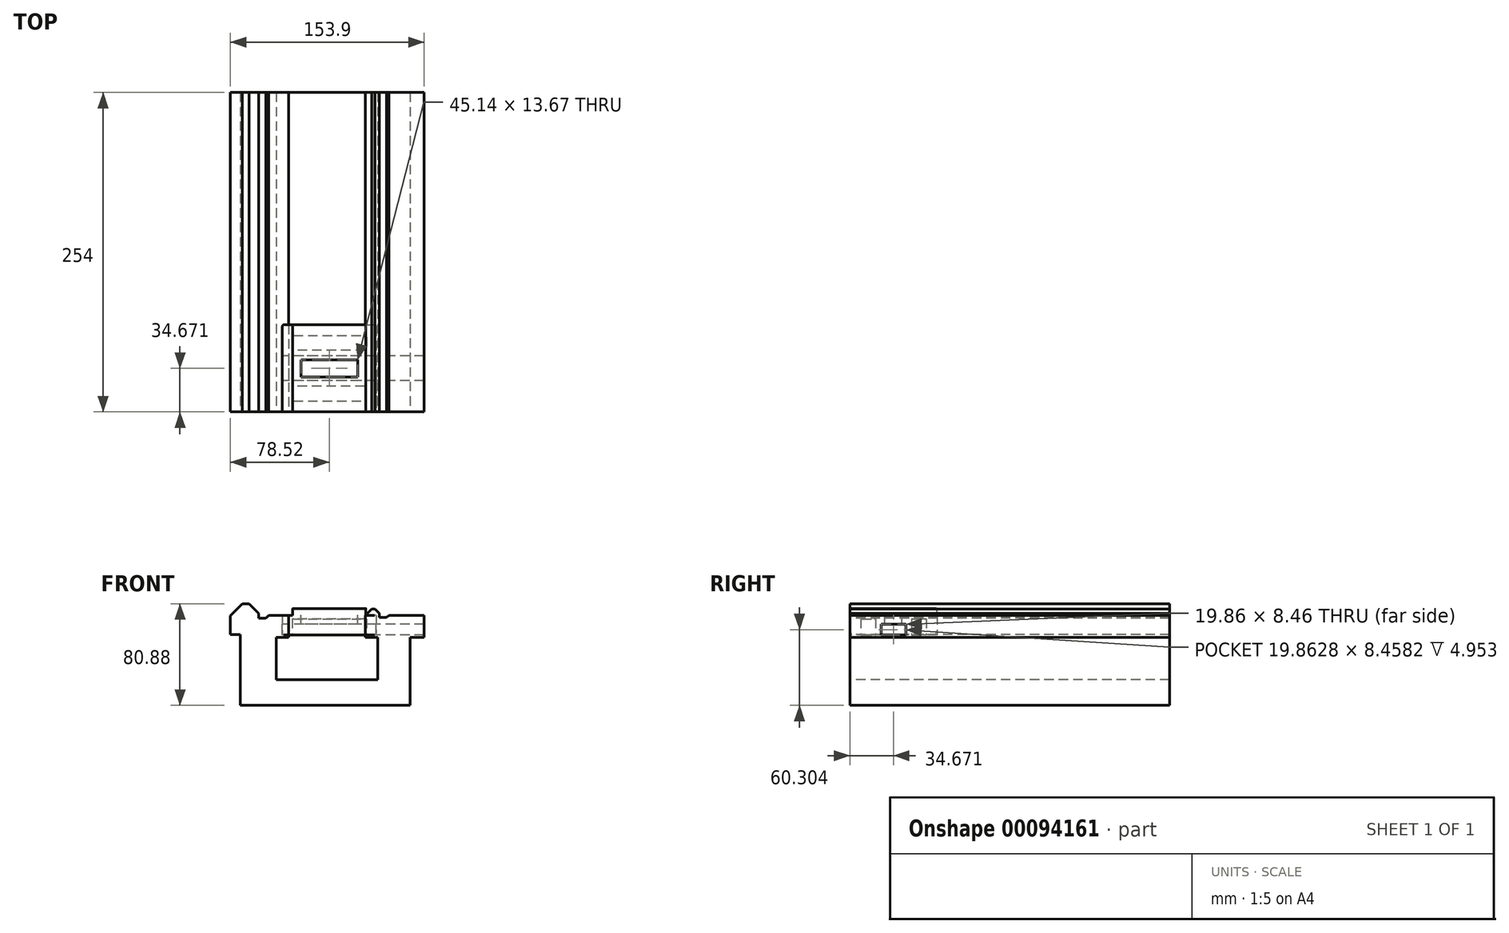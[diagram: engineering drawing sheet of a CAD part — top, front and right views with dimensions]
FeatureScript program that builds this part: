
annotation { "Feature Type Name" : "Feature", "Feature Type Description" : "" }
export const myFeature = defineFeature(function(context is Context, id is Id, definition is map)
    precondition{}
    {
        {
            var Q0;
            Q0=qCreatedBy(makeId("Front.planeOp"),FACE);
            var sketch = newSketch(context, id + "F0", { "sketchPlane" : qUnion([Q0])});
            skLineSegment(sketch, "E0", {"start": v(28.67, -0.1) * mm, "end": v(28.67, -17.38) * mm, "construction": true});
            skLineSegment(sketch, "E1", {"start": v(-32.32, -0.14) * mm, "end": v(-32.17, -17.38) * mm});
            skLineSegment(sketch, "E2", {"start": v(-32.17, -17.38) * mm, "end": v(-42.05, -17.38) * mm});
            skLineSegment(sketch, "E3", {"start": v(-32.32, -0.14) * mm, "end": v(-48.22, -0.14) * mm});
            skLineSegment(sketch, "E4", {"start": v(-48.22, -0.14) * mm, "end": v(-50.4, -2.17) * mm});
            skLineSegment(sketch, "E5", {"start": v(-50.4, -2.17) * mm, "end": v(-56.12, -2.17) * mm});
            skLineSegment(sketch, "E6", {"start": v(-56.12, -2.17) * mm, "end": v(-56.12, 1.62) * mm});
            skLineSegment(sketch, "E7", {"start": v(-56.12, 1.62) * mm, "end": v(-63.76, 9.26) * mm});
            skLineSegment(sketch, "E8", {"start": v(-70.74, -15.12) * mm, "end": v(-78.52, -15.12) * mm});
            skLineSegment(sketch, "E9", {"start": v(-69, 9.26) * mm, "end": v(-63.76, 9.26) * mm, "construction": true});
            skLineSegment(sketch, "E10", {"start": v(-63.76, 9.26) * mm, "end": v(-69, 9.26) * mm});
            skLineSegment(sketch, "E11", {"start": v(-69, 9.26) * mm, "end": v(-78.52, -0.27) * mm});
            skLineSegment(sketch, "E12", {"start": v(-70.74, -15.12) * mm, "end": v(-70.74, -40.32) * mm});
            skLineSegment(sketch, "E13", {"start": v(28.67, -17.38) * mm, "end": v(38.52, -17.38) * mm, "construction": true});
            skLineSegment(sketch, "E14", {"start": v(33.66, 4.9) * mm, "end": v(36.3, 4.9) * mm, "construction": true});
            skLineSegment(sketch, "E15", {"start": v(39.74, -1.69) * mm, "end": v(39.74, 1.46) * mm, "construction": true});
            skLineSegment(sketch, "E16", {"start": v(45.6, -1.69) * mm, "end": v(39.74, -1.69) * mm, "construction": true});
            skLineSegment(sketch, "E17", {"start": v(28.67, -17.38) * mm, "end": v(38.52, -17.38) * mm});
            skLineSegment(sketch, "E18", {"start": v(38.52, -17.38) * mm, "end": v(38.52, -19.45) * mm});
            skLineSegment(sketch, "E19", {"start": v(28.67, -17.38) * mm, "end": v(28.67, -0.1) * mm});
            skLineSegment(sketch, "E20", {"start": v(33.66, 4.9) * mm, "end": v(36.3, 4.9) * mm});
            skLineSegment(sketch, "E21", {"start": v(39.74, 1.46) * mm, "end": v(39.74, -1.69) * mm});
            skLineSegment(sketch, "E22", {"start": v(39.74, -1.69) * mm, "end": v(45.6, -1.69) * mm});
            skLineSegment(sketch, "E23", {"start": v(75.38, -1.69) * mm, "end": v(75.38, -17.38) * mm});
            skLineSegment(sketch, "E24", {"start": v(75.38, -17.38) * mm, "end": v(64.28, -17.38) * mm});
            skLineSegment(sketch, "E25", {"start": v(64.28, -17.38) * mm, "end": v(64.28, -37.3) * mm});
            skLineSegment(sketch, "E26", {"start": v(64.28, -37.3) * mm, "end": v(64.28, -51.73) * mm});
            skLineSegment(sketch, "E27", {"start": v(-70.74, -51.73) * mm, "end": v(-70.74, -40.32) * mm});
            skLineSegment(sketch, "E28", {"start": v(38.52, -19.45) * mm, "end": v(38.52, -51.23) * mm});
            skLineSegment(sketch, "E29", {"start": v(38.52, -51.23) * mm, "end": v(-42.05, -51.23) * mm});
            skLineSegment(sketch, "E30", {"start": v(-42.05, -51.23) * mm, "end": v(-42.05, -17.38) * mm});
            skLineSegment(sketch, "E31", {"start": v(-70.74, -51.73) * mm, "end": v(-70.74, -71.62) * mm});
            skLineSegment(sketch, "E32", {"start": v(-70.74, -71.62) * mm, "end": v(64.28, -71.62) * mm});
            skLineSegment(sketch, "E33", {"start": v(64.28, -71.62) * mm, "end": v(64.28, -51.73) * mm});
            skPoint(sketch, "E34.orphan", {"position": v(18.52, -51.23) * mm});
            skLineSegment(sketch, "E35.trimOffspring", {"start": v(64.28, -17.38) * mm, "end": v(75.38, -17.38) * mm, "construction": true});
            skLineSegment(sketch, "E36", {"start": v(33.66, 4.9) * mm, "end": v(28.67, -0.1) * mm});
            skLineSegment(sketch, "E37", {"start": v(36.3, 4.9) * mm, "end": v(39.74, 1.46) * mm});
            skPoint(sketch, "E38", {"position": v(28.67, -0.1) * mm});
            skPoint(sketch, "E39", {"position": v(39.74, 1.46) * mm});
            skLineSegment(sketch, "E40", {"start": v(45.6, -1.69) * mm, "end": v(47.3, 0.02) * mm});
            skLineSegment(sketch, "E41", {"start": v(73.53, 0.02) * mm, "end": v(47.3, 0.02) * mm});
            skLineSegment(sketch, "E42", {"start": v(75.38, -1.69) * mm, "end": v(75.38, 0.02) * mm});
            skLineSegment(sketch, "E43", {"start": v(75.38, 0.02) * mm, "end": v(73.53, 0.02) * mm});
            skLineSegment(sketch, "E44", {"start": v(-78.52, -15.12) * mm, "end": v(-78.52, -0.27) * mm});
            skSolve(sketch);
        }
        {
            var Q0;
            Q0=makeQuery(id+"F0.imprint","IMPRINT",FACE,{"disambiguationData":[TD([[makeQuery(id+"F0.imprint","IMPRINT",EDGE,{"derivedFrom":sQuery(id+"F0.wireOp",EDGE,"E1")}),-1.0]])]});
            extrude(context, id + "F1", {"entities" : qUnion([Q0]), "oppositeDirection" : true, "depth" : 254 * mm});
        }
        {
            var Q0;
            Q0=qCreatedBy(makeId("Front.planeOp"),FACE);
            var sketch = newSketch(context, id + "F2", { "sketchPlane" : qUnion([Q0])});
            skPoint(sketch, "E45.middle", {"position": v(0, 0) * mm});
            skLineSegment(sketch, "E46.bottom", {"start": v(-37.21, 0) * mm, "end": v(-29.08, 0) * mm});
            skLineSegment(sketch, "E46.top", {"start": v(-37.21, -15.54) * mm, "end": v(37.21, -15.54) * mm});
            skLineSegment(sketch, "E46.left", {"start": v(-37.21, 0) * mm, "end": v(-37.21, -15.54) * mm});
            skLineSegment(sketch, "E46.right", {"start": v(37.21, 0) * mm, "end": v(37.21, -15.54) * mm});
            skLineSegment(sketch, "E47.top", {"start": v(-29.08, 5.38) * mm, "end": v(29.08, 5.38) * mm});
            skLineSegment(sketch, "E47.left", {"start": v(-29.08, 0) * mm, "end": v(-29.08, 5.38) * mm});
            skLineSegment(sketch, "E47.right", {"start": v(29.08, 0) * mm, "end": v(29.08, 5.38) * mm});
            skLineSegment(sketch, "E48.trimOffspring", {"start": v(29.08, 0) * mm, "end": v(37.21, 0) * mm});
            skSolve(sketch);
        }
        {
            var Q0;
            Q0=makeQuery(id+"F2.imprint","IMPRINT",FACE,{"disambiguationData":[TD([[makeQuery(id+"F2.imprint","IMPRINT",EDGE,{"derivedFrom":sQuery(id+"F2.wireOp",EDGE,"E46.bottom")}),-1.0]])]});
            extrude(context, id + "F3", {"entities" : qUnion([Q0]), "oppositeDirection" : true, "depth" : 69.34 * mm});
        }
        {
            var Q0;
            Q0=makeQuery(id+"F3.opExtrude","SWEPT_FACE",FACE,{"disambiguationData":[OSD([sQuery(id+"F2.wireOp",EDGE,"E46.left")])]});
            var sketch = newSketch(context, id + "F4", { "sketchPlane" : qUnion([Q0])});
            skLineSegment(sketch, "E49.bottom", {"start": v(-44.6, -15.54) * mm, "end": v(-24.74, -15.54) * mm});
            skLineSegment(sketch, "E49.top", {"start": v(-44.6, -7.09) * mm, "end": v(-24.74, -7.09) * mm});
            skLineSegment(sketch, "E49.left", {"start": v(-44.6, -15.54) * mm, "end": v(-44.6, -7.09) * mm});
            skLineSegment(sketch, "E49.right", {"start": v(-24.74, -15.54) * mm, "end": v(-24.74, -7.09) * mm});
            skPoint(sketch, "E50", {"position": v(-34.67, -15.54) * mm});
            skSolve(sketch);
        }
        {
            var Q0;
            Q0=makeQuery(id+"F4.imprint","IMPRINT",FACE,{"disambiguationData":[TD([[makeQuery(id+"F4.imprint","IMPRINT",EDGE,{"derivedFrom":sQuery(id+"F4.wireOp",EDGE,"E49.bottom")}),1.0]])]});
            extrude(context, id + "F5", {"entities" : qUnion([Q0]), "operationType" : NewBodyOperationType.REMOVE, "endBound" : BoundingType.THROUGH_ALL, "oppositeDirection" : true, "depth" : 25.4 * mm});
        }
        {
            var Q0;
            Q0=makeQuery(id+"F3.opExtrude","SWEPT_FACE",FACE,{"disambiguationData":[OSD([sQuery(id+"F2.wireOp",EDGE,"E47.top")])]});
            var sketch = newSketch(context, id + "F6", { "sketchPlane" : qUnion([Q0])});
            skLineSegment(sketch, "E51.bottom", {"start": v(22.57, 41.5) * mm, "end": v(-22.57, 41.5) * mm});
            skLineSegment(sketch, "E51.top", {"start": v(22.57, 27.84) * mm, "end": v(-22.57, 27.84) * mm});
            skLineSegment(sketch, "E51.left", {"start": v(22.57, 41.5) * mm, "end": v(22.57, 27.84) * mm});
            skLineSegment(sketch, "E51.right", {"start": v(-22.57, 41.5) * mm, "end": v(-22.57, 27.84) * mm});
            skSolve(sketch);
        }
        {
            var Q0;
            Q0=makeQuery(id+"F6.imprint","IMPRINT",FACE,{"disambiguationData":[TD([[makeQuery(id+"F6.imprint","IMPRINT",EDGE,{"derivedFrom":sQuery(id+"F6.wireOp",EDGE,"E51.bottom")}),1.0]])]});
            extrude(context, id + "F7", {"entities" : qUnion([Q0]), "operationType" : NewBodyOperationType.REMOVE, "endBound" : BoundingType.UP_TO_NEXT, "oppositeDirection" : true, "depth" : 25.4 * mm});
        }
        {
            var Q0;
            {var subQ2=sQuery(id+"F2.wireOp",EDGE,"E46.top");Q0=makeQuery(id+"F5.boolean.opBoolean","SPLIT",FACE,{"disambiguationData":[TD([makeQuery(id+"F5.opExtrude","SWEPT_FACE",FACE,{"disambiguationData":[OSD([sQuery(id+"F4.wireOp",EDGE,"E49.right")])]})])],"derivedFrom":makeQuery(id+"F3.opExtrude","SWEPT_FACE",FACE,{"disambiguationData":[OSD([subQ2])]})});}
            var sketch = newSketch(context, id + "F8", { "sketchPlane" : qUnion([Q0])});
            skLineSegment(sketch, "E52", {"start": v(29.53, -8.64) * mm, "end": v(29.53, -20.34) * mm});
            skLineSegment(sketch, "E53", {"start": v(29.53, -20.34) * mm, "end": v(-29.53, -20.34) * mm});
            skLineSegment(sketch, "E54", {"start": v(-29.53, -20.34) * mm, "end": v(-29.53, -8.64) * mm});
            skLineSegment(sketch, "E55", {"start": v(-29.53, -8.64) * mm, "end": v(29.53, -8.64) * mm});
            skPoint(sketch, "E56.end.orphan", {"position": v(-9.76, -8.64) * mm});
            skPoint(sketch, "E57.end.orphan", {"position": v(-29.53, -13.61) * mm});
            skPoint(sketch, "E58.end.orphan", {"position": v(3.76, -20.34) * mm});
            skPoint(sketch, "E59.start.orphan", {"position": v(37.21, -8.64) * mm});
            skSolve(sketch);
        }
        {
            var Q0;
            {var subQ2=sQuery(id+"F2.wireOp",EDGE,"E46.top");Q0=makeQuery(id+"F5.boolean.opBoolean","SPLIT",FACE,{"disambiguationData":[TD([makeQuery(id+"F5.opExtrude","SWEPT_FACE",FACE,{"disambiguationData":[OSD([sQuery(id+"F4.wireOp",EDGE,"E49.left")])]})])],"derivedFrom":makeQuery(id+"F3.opExtrude","SWEPT_FACE",FACE,{"disambiguationData":[OSD([subQ2])]})});}
            var sketch = newSketch(context, id + "F9", { "sketchPlane" : qUnion([Q0])});
            skLineSegment(sketch, "E60", {"start": v(-29.55, -60.77) * mm, "end": v(29.7, -60.77) * mm});
            skLineSegment(sketch, "E61", {"start": v(29.7, -48.96) * mm, "end": v(-29.55, -48.96) * mm});
            skLineSegment(sketch, "E62", {"start": v(-29.55, -48.96) * mm, "end": v(-29.55, -60.77) * mm});
            skLineSegment(sketch, "E63", {"start": v(29.7, -60.77) * mm, "end": v(29.7, -48.96) * mm});
            skSolve(sketch);
        }
        {
            var Q0;
            Q0=makeQuery(id+"F8.imprint","IMPRINT",FACE,{"disambiguationData":[TD([[makeQuery(id+"F8.imprint","IMPRINT",EDGE,{"derivedFrom":sQuery(id+"F8.wireOp",EDGE,"E52")}),-1.0]])]});
            var Q1;
            Q1=makeQuery(id+"F9.imprint","IMPRINT",FACE,{"disambiguationData":[TD([[makeQuery(id+"F9.imprint","IMPRINT",EDGE,{"derivedFrom":sQuery(id+"F9.wireOp",EDGE,"E60")}),1.0]])]});
            extrude(context, id + "F10", {"entities" : qUnion([Q0, Q1]), "operationType" : NewBodyOperationType.REMOVE, "oppositeDirection" : true, "depth" : 12.7 * mm});
        }
        {
            var Q0;
            Q0=makeQuery(id+"F10.boolean.opBoolean","COPY",EDGE,{"derivedFrom":makeQuery(id+"F10.opExtrude","SWEPT_EDGE",EDGE,{"disambiguationData":[OSD([sQuery(id+"F9.wireOp",EDGE,"E61"),sQuery(id+"F9.wireOp",EDGE,"E62")])]})});
            var Q1;
            Q1=makeQuery(id+"F10.boolean.opBoolean","COPY",EDGE,{"derivedFrom":makeQuery(id+"F10.opExtrude","SWEPT_EDGE",EDGE,{"disambiguationData":[OSD([sQuery(id+"F9.wireOp",EDGE,"E60"),sQuery(id+"F9.wireOp",EDGE,"E62")])]})});
            var Q2;
            Q2=makeQuery(id+"F10.boolean.opBoolean","COPY",EDGE,{"derivedFrom":makeQuery(id+"F10.opExtrude","SWEPT_EDGE",EDGE,{"disambiguationData":[OSD([sQuery(id+"F8.wireOp",EDGE,"E53"),sQuery(id+"F8.wireOp",EDGE,"E54")])]})});
            var Q3;
            Q3=makeQuery(id+"F10.boolean.opBoolean","COPY",EDGE,{"derivedFrom":makeQuery(id+"F10.opExtrude","SWEPT_EDGE",EDGE,{"disambiguationData":[OSD([sQuery(id+"F8.wireOp",EDGE,"E54"),sQuery(id+"F8.wireOp",EDGE,"E55")])]})});
            var Q4;
            Q4=makeQuery(id+"F10.boolean.opBoolean","COPY",EDGE,{"derivedFrom":makeQuery(id+"F10.opExtrude","SWEPT_EDGE",EDGE,{"disambiguationData":[OSD([sQuery(id+"F8.wireOp",EDGE,"E52"),sQuery(id+"F8.wireOp",EDGE,"E55")])]})});
            var Q5;
            Q5=makeQuery(id+"F10.boolean.opBoolean","COPY",EDGE,{"derivedFrom":makeQuery(id+"F10.opExtrude","SWEPT_EDGE",EDGE,{"disambiguationData":[OSD([sQuery(id+"F8.wireOp",EDGE,"E52"),sQuery(id+"F8.wireOp",EDGE,"E53")])]})});
            var Q6;
            Q6=makeQuery(id+"F10.boolean.opBoolean","COPY",EDGE,{"derivedFrom":makeQuery(id+"F10.opExtrude","SWEPT_EDGE",EDGE,{"disambiguationData":[OSD([sQuery(id+"F9.wireOp",EDGE,"E60"),sQuery(id+"F9.wireOp",EDGE,"E63")])]})});
            var Q7;
            Q7=makeQuery(id+"F10.boolean.opBoolean","COPY",EDGE,{"derivedFrom":makeQuery(id+"F10.opExtrude","SWEPT_EDGE",EDGE,{"disambiguationData":[OSD([sQuery(id+"F9.wireOp",EDGE,"E61"),sQuery(id+"F9.wireOp",EDGE,"E63")])]})});
            fillet(context, id + "F11", {"entities" : qUnion([Q0, Q1, Q2, Q3, Q4, Q5, Q6, Q7]), "radius" : 1.27 * mm, "tangentPropagation" : true, "allowEdgeOverflow" : false});
        }
        {
            var Q0;
            Q0=makeQuery(id+"F3.opExtrude","CAP_EDGE",EDGE,{"disambiguationData":[OSD([sQuery(id+"F2.wireOp",EDGE,"E46.right")])],"isStart":false});
            var Q1;
            Q1=makeQuery(id+"F3.opExtrude","CAP_EDGE",EDGE,{"disambiguationData":[OSD([sQuery(id+"F2.wireOp",EDGE,"E46.left")])],"isStart":false});
            var Q2;
            Q2=makeQuery(id+"F3.opExtrude","CAP_EDGE",EDGE,{"disambiguationData":[OSD([sQuery(id+"F2.wireOp",EDGE,"E46.right")])],"isStart":true});
            var Q3;
            Q3=makeQuery(id+"F3.opExtrude","CAP_EDGE",EDGE,{"disambiguationData":[OSD([sQuery(id+"F2.wireOp",EDGE,"E46.left")])],"isStart":true});
            var Q4;
            Q4=makeQuery(id+"F3.opExtrude","CAP_EDGE",EDGE,{"disambiguationData":[OSD([sQuery(id+"F2.wireOp",EDGE,"E47.top")])],"isStart":true});
            var Q5;
            Q5=makeQuery(id+"F3.opExtrude","CAP_EDGE",EDGE,{"disambiguationData":[OSD([sQuery(id+"F2.wireOp",EDGE,"E47.top")])],"isStart":false});
            var Q6;
            {var subQ0=sQuery(id+"F2.wireOp",EDGE,"E46.left");var subQ1=sQuery(id+"F2.wireOp",EDGE,"E46.top");Q6=makeQuery(id+"F5.boolean.opBoolean","SPLIT",EDGE,{"disambiguationData":[TD([makeQuery(id+"F5.opExtrude","SWEPT_FACE",FACE,{"disambiguationData":[OSD([sQuery(id+"F4.wireOp",EDGE,"E49.left")])]})])],"derivedFrom":makeQuery(id+"F3.opExtrude","SWEPT_EDGE",EDGE,{"disambiguationData":[OSD([subQ1,subQ0])]})});}
            var Q7;
            {var subQ0=sQuery(id+"F2.wireOp",EDGE,"E46.left");var subQ1=sQuery(id+"F2.wireOp",EDGE,"E46.top");Q7=makeQuery(id+"F5.boolean.opBoolean","SPLIT",EDGE,{"disambiguationData":[TD([makeQuery(id+"F5.opExtrude","SWEPT_FACE",FACE,{"disambiguationData":[OSD([sQuery(id+"F4.wireOp",EDGE,"E49.right")])]})])],"derivedFrom":makeQuery(id+"F3.opExtrude","SWEPT_EDGE",EDGE,{"disambiguationData":[OSD([subQ1,subQ0])]})});}
            var Q8;
            {var subQ0=sQuery(id+"F2.wireOp",EDGE,"E46.right");var subQ1=sQuery(id+"F2.wireOp",EDGE,"E46.top");Q8=makeQuery(id+"F5.boolean.opBoolean","SPLIT",EDGE,{"disambiguationData":[TD([makeQuery(id+"F5.opExtrude","SWEPT_FACE",FACE,{"disambiguationData":[OSD([sQuery(id+"F4.wireOp",EDGE,"E49.right")])]})])],"derivedFrom":makeQuery(id+"F3.opExtrude","SWEPT_EDGE",EDGE,{"disambiguationData":[OSD([subQ1,subQ0])]})});}
            var Q9;
            {var subQ0=sQuery(id+"F2.wireOp",EDGE,"E46.right");var subQ1=sQuery(id+"F2.wireOp",EDGE,"E46.top");Q9=makeQuery(id+"F5.boolean.opBoolean","SPLIT",EDGE,{"disambiguationData":[TD([makeQuery(id+"F5.opExtrude","SWEPT_FACE",FACE,{"disambiguationData":[OSD([sQuery(id+"F4.wireOp",EDGE,"E49.left")])]})])],"derivedFrom":makeQuery(id+"F3.opExtrude","SWEPT_EDGE",EDGE,{"disambiguationData":[OSD([subQ1,subQ0])]})});}
            var Q10;
            Q10=makeQuery(id+"F10.boolean.opBoolean","COPY",EDGE,{"derivedFrom":makeQuery(id+"F10.opExtrude","CAP_EDGE",EDGE,{"disambiguationData":[OSD([sQuery(id+"F8.wireOp",EDGE,"E53")])],"isStart":true})});
            var Q11;
            Q11=makeQuery(id+"F10.boolean.opBoolean","COPY",EDGE,{"derivedFrom":makeQuery(id+"F10.opExtrude","CAP_EDGE",EDGE,{"disambiguationData":[OSD([sQuery(id+"F9.wireOp",EDGE,"E60")])],"isStart":true})});
            fillet(context, id + "F12", {"entities" : qUnion([Q0, Q1, Q2, Q3, Q4, Q5, Q6, Q7, Q8, Q9, Q10, Q11]), "radius" : 1.27 * mm, "tangentPropagation" : true, "allowEdgeOverflow" : false});
        }
    });
